# Revit family: STH21729BR_30_STH21729PTO_30
name_source: partatom
category: Luminárias
units: mm (PartAtom-declared; Revit-internal decimal feet)

## family parameters
Compartilhado = Não
Corte com vazios quando carregada = Não
Cota do conector redondo = Utilizar diâmetro
Fonte luminosa = Sim
Hospedeiro = Parede
Manter orientação da anotação = Não
Número OmniClass = 23.80.70.00
Ponto de cálculo do ambiente = Não
Sempre na vertical = Sim
Tipo de parte = Normal
Título OmniClass = Lighting

## types (2) — shared parameters
Altura = 0.07 m
Comprimento = 0.04 m
Dimerização = Não dimerizável
Fabricante = Stella
Filtro de cor = 16777215
Fluxo Luminoso = 10 lm
Grau de proteção (IP) = IP65
IRC (Índice de reprodução de cores) = >80
Largura = 0.02 m
Luminoso = Luminoso - 3000K
Modelo = Wall Micro
Potência = 3 W
Temperatura da cor (K) = 3000 K
Tensão Elétrica = 100V-240V
Troca de temperatura da cor de lâmpada com esmaecimento = <Nenhum>
URL = https://stella.com.br
Ângulo de Abertura = 4°
Ângulo de inclinação = 90.00°
zero-valued in all types: Elevação padrão

## per-type parameters (varying)
| type | Arquivo de rede fotométrica | Estrutura | Referência |
| STH21729BR/30 - BRANCO - BIVOLT - 3000K - 10lm | STELLA - STH21729BR-30 - WALL MICRO FACHO FECHADO.ies | Al - Branco | STH21729BR/30 |
| STH21729PTO/30 - PRETO - BIVOLT - 3000K - 10lm | STELLA - STH21729PTO-30 - WALL MICRO FACHO FECHADO.ies | Al - Preto | STH21729PTO/30 |
